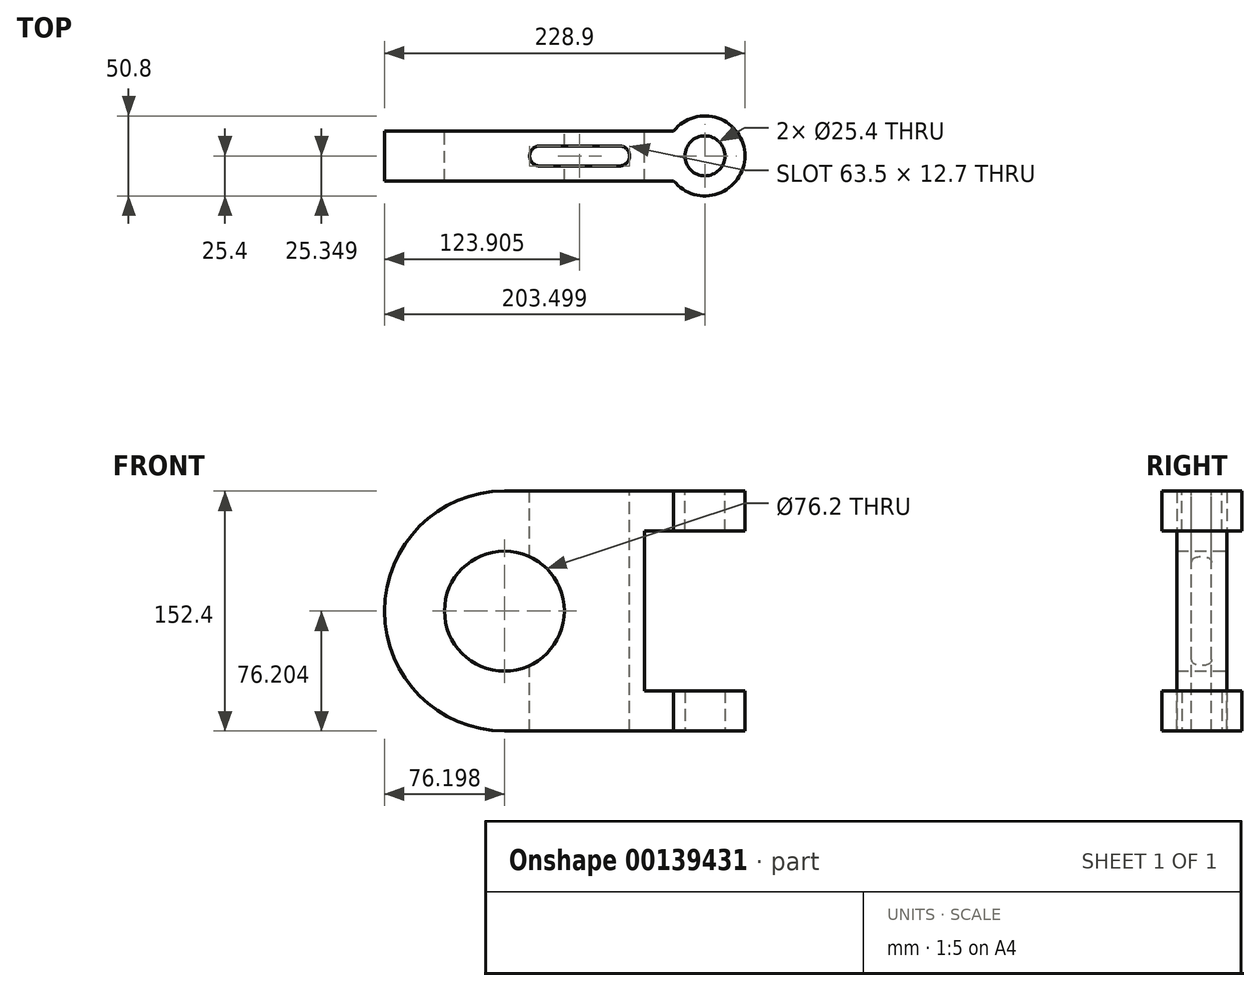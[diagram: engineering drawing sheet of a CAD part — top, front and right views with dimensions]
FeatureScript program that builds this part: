
annotation { "Feature Type Name" : "Feature", "Feature Type Description" : "" }
export const myFeature = defineFeature(function(context is Context, id is Id, definition is map)
    precondition{}
    {
        {
            var Q0;
            Q0=qCreatedBy(makeId("Front.planeOp"),FACE);
            var sketch = newSketch(context, id + "F0", { "sketchPlane" : qUnion([Q0])});
            skLineSegment(sketch, "E0", {"start": v(-36.61, 70.37) * mm, "end": v(70.86, 70.37) * mm});
            skLineSegment(sketch, "E1", {"start": v(-36.61, -82.03) * mm, "end": v(70.86, -82.03) * mm});
            skArc(sketch, "E2", {"start": v(-36.61, 70.37) * mm, "mid": v(-112.81, -5.83) * mm, "end": v(-36.61, -82.03) * mm});
            skLineSegment(sketch, "E3", {"start": v(70.86, 70.37) * mm, "end": v(70.86, 44.97) * mm});
            skLineSegment(sketch, "E4", {"start": v(70.86, -82.03) * mm, "end": v(70.86, -56.63) * mm});
            skLineSegment(sketch, "E5", {"start": v(70.86, 44.97) * mm, "end": v(52.29, 44.97) * mm});
            skLineSegment(sketch, "E6", {"start": v(70.86, -56.63) * mm, "end": v(52.29, -56.63) * mm});
            skLineSegment(sketch, "E7", {"start": v(52.29, 44.97) * mm, "end": v(52.29, -56.63) * mm});
            skCircle(sketch, "E8", {"center": v(-36.61, -5.83) * mm, "radius": 38.1 * mm});
            skSolve(sketch);
        }
        {
            var Q0;
            Q0 = qSketchRegion(id + "F0", true);
            extrude(context, id + "F1", {"entities" : qUnion([Q0]), "endBound" : BoundingType.SYMMETRIC, "depth" : 31.75 * mm});
        }
        {
            var Q0;
            Q0=makeQuery(id+"F1.opExtrude","SWEPT_FACE",FACE,{"disambiguationData":[OSD([sQuery(id+"F0.wireOp",EDGE,"E0")])]});
            var sketch = newSketch(context, id + "F2", { "sketchPlane" : qUnion([Q0])});
            skLineSegment(sketch, "E9", {"start": v(-14.3, 6.3) * mm, "end": v(36.5, 6.3) * mm});
            skLineSegment(sketch, "E10", {"start": v(-14.3, -6.4) * mm, "end": v(36.5, -6.4) * mm});
            skArc(sketch, "E11", {"start": v(-14.3, 6.3) * mm, "mid": v(-20.65, -0.05) * mm, "end": v(-14.3, -6.4) * mm});
            skArc(sketch, "E12", {"start": v(36.5, -6.4) * mm, "mid": v(42.85, -0.05) * mm, "end": v(36.5, 6.3) * mm});
            skSolve(sketch);
        }
        {
            var Q0;
            Q0 = qSketchRegion(id + "F2", true);
            extrude(context, id + "F3", {"entities" : qUnion([Q0]), "operationType" : NewBodyOperationType.REMOVE, "oppositeDirection" : true, "depth" : 152.4 * mm});
        }
        {
            var Q0;
            Q0=makeQuery(id+"F1.opExtrude","SWEPT_FACE",FACE,{"disambiguationData":[OSD([sQuery(id+"F0.wireOp",EDGE,"E0")])]});
            var sketch = newSketch(context, id + "F4", { "sketchPlane" : qUnion([Q0])});
            skCircle(sketch, "E13", {"center": v(90.69, 0) * mm, "radius": 12.7 * mm});
            skArc(sketch, "E14", {"start": v(70.86, -15.88) * mm, "mid": v(116.09, 0) * mm, "end": v(70.86, 15.88) * mm});
            skPoint(sketch, "E15", {"position": v(70.86, 0) * mm});
            skSolve(sketch);
        }
        {
            var Q0;
            Q0=makeQuery(id+"F4.imprint","IMPRINT",FACE,{"disambiguationData":[TD([[makeQuery(id+"F4.imprint","IMPRINT",EDGE,{"derivedFrom":sQuery(id+"F4.wireOp",EDGE,"a24OTElN-C5pQ-tEPG-fSUK-ja8BYXoe7w24")}),1.0]])]});
            var Q1;
            Q1=makeQuery(id+"F4.imprint","IMPRINT",FACE,{"disambiguationData":[TD([[makeQuery(id+"F4.imprint","IMPRINT",EDGE,{"derivedFrom":sQuery(id+"F4.wireOp",EDGE,"E13")}),-1.0]])]});
            extrude(context, id + "F5", {"entities" : qUnion([Q0, Q1]), "oppositeDirection" : true, "depth" : 25.4 * mm});
        }
        {
            var Q0;
            Q0=makeQuery(id+"F1.opExtrude","CAP_VERTEX",VERTEX,{"disambiguationData":[OSD([sQuery(id+"F0.wireOp",EDGE,"E5"),sQuery(id+"F0.wireOp",EDGE,"E7")])],"isStart":false});
            var Q1;
            Q1=makeQuery(id+"F1.opExtrude","CAP_VERTEX",VERTEX,{"disambiguationData":[OSD([sQuery(id+"F0.wireOp",EDGE,"E6"),sQuery(id+"F0.wireOp",EDGE,"E7")])],"isStart":false});
            cPlane(context, id + "F6", {"entities" : qUnion([Q0, Q1]), "cplaneType" : CPlaneType.MID_PLANE, "offset" : 25.4 * mm, "width" : 152.4 * mm, "height" : 152.4 * mm});
        }
        {
            var Q0;
            Q0=makeQuery(id+"F5.opExtrude","SWEPT_BODY",BODY,{"disambiguationData":[OSD([sQuery(id+"F0.wireOp",EDGE,"E0"),sQuery(id+"F0.wireOp",EDGE,"E3"),sQuery(id+"F4.wireOp",EDGE,"a24OTElN-C5pQ-tEPG-fSUK-ja8BYXoe7w24"),sQuery(id+"F4.wireOp",EDGE,"E13")])]});
            var Q1;
            Q1=qCreatedBy(id+"F6.planeOp",FACE);
            mirror(context, id + "F7", {"operationType" : NewBodyOperationType.ADD, "entities" : qUnion([Q0]), "mirrorPlane" : qUnion([Q1])});
        }
    });
